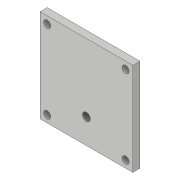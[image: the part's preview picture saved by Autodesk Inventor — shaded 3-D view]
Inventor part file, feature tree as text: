
AUTODESK INVENTOR PART (.ipt)
format: ipt  version: 2019 (Build 230136000, 136)  size: 108,032 bytes
history: native  units: in
note: dims shown in document units (in); Inventor stores cm internally (conversion verified against a paired STEP export)
features: extrude x3, sketch x3, thread x1
ambient origin geometry x8: Origin, YZ Plane, XZ Plane, XY Plane, X Axis, Y Axis, Z Axis, Center Point
bodies: Solid1 (feature_tree)
feature tree (7):
  extrude  "Extrusion1"  Depth=5.1181in
  extrude  "Extrusion2"  Depth=0.3937in
  extrude  "Extrusion3"  Depth=0.3937in
  thread  "Thread1"  [1 undecoded]
  sketch  "Sketch1"  dims[d0=5.1181in d1=5.1181in]
  sketch  "Sketch2"  dims[d2=0.3937in d3=0.0in d4=0.3937in]
  sketch  "Sketch3"  dims[d5=5.1181in d6=4.3307in d7=0.3937in d8=0.3937in d9=5.1181in d10=0.3937in d11=0.3937in d12=0.3937in d13=0.3937in d14=0.0in d15=0.0in d16=2.5591in d17=1.378in d18=1.378in d19=0.4331in d20=0.0in d21=0.0in d22=0.3937in d23=0.0in]
note: 1 required parameter value undecoded (feature->parameter linkage not recoverable at this tier; creation-order binding heuristic only, values carry confidence <= 0.55)
